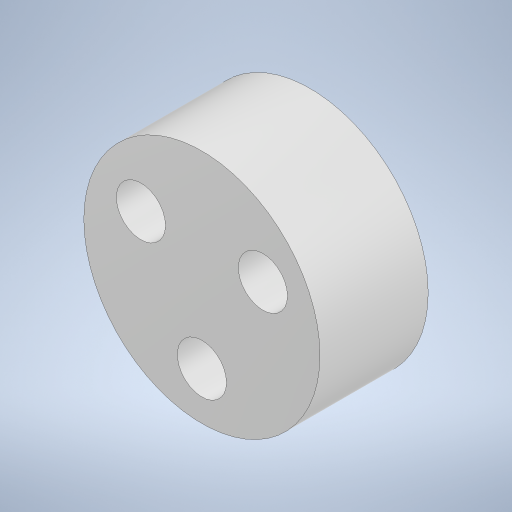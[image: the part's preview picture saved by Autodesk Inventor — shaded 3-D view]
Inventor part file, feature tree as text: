
AUTODESK INVENTOR PART (.ipt)
format: ipt  version: 2023.1 (Build 271208000, 208)  size: 231,424 bytes
history: native  units: mm
features: extrude x1, sketch x1
ambient origin geometry x8: Origin, YZ Plane, XZ Plane, XY Plane, X Axis, Y Axis, Z Axis, Center Point
bodies: Solid1 (feature_tree)
feature tree (2):
  extrude  "Extrusion1"  [1 undecoded]
  sketch  "Sketch1"  dims[d0=12.0mm d1=5.5mm d2=0.0mm]
note: 1 required parameter value undecoded (feature->parameter linkage not recoverable at this tier; creation-order binding heuristic only, values carry confidence <= 0.55)
